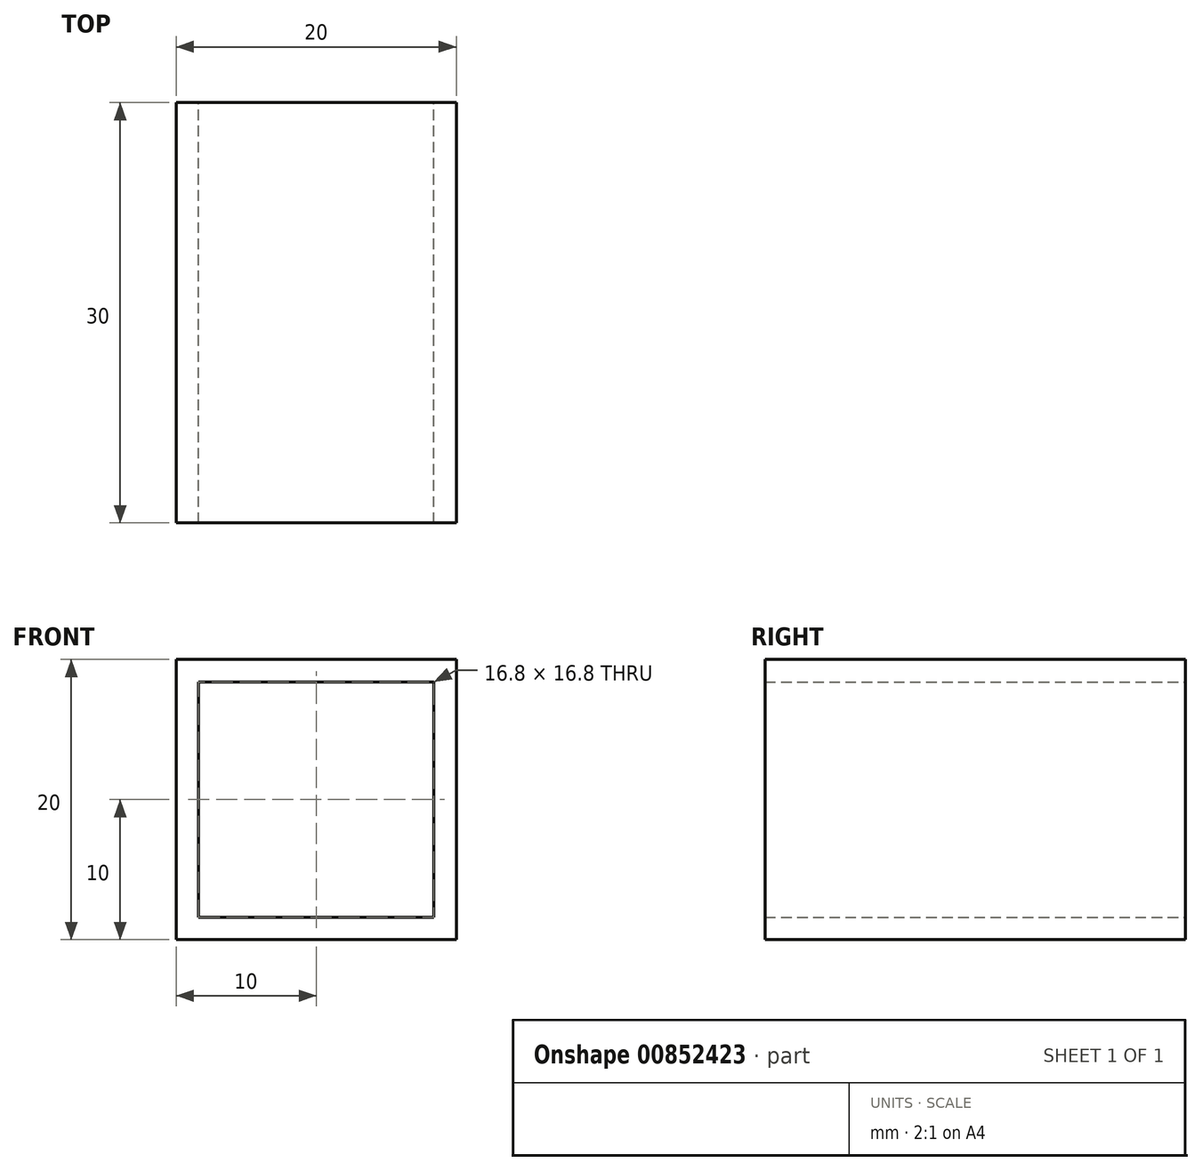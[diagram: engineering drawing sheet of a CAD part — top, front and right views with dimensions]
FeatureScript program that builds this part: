
annotation { "Feature Type Name" : "Feature", "Feature Type Description" : "" }
export const myFeature = defineFeature(function(context is Context, id is Id, definition is map)
    precondition{}
    {
        {
            var Q0;
            Q0=qCreatedBy(makeId("Front.planeOp"),FACE);
            var sketch = newSketch(context, id + "F0", { "sketchPlane" : qUnion([Q0])});
            skLineSegment(sketch, "E0.bottom", {"start": v(10, 10) * mm, "end": v(-10, 10) * mm});
            skLineSegment(sketch, "E0.top", {"start": v(10, -10) * mm, "end": v(-10, -10) * mm});
            skLineSegment(sketch, "E0.left", {"start": v(10, 10) * mm, "end": v(10, -10) * mm});
            skLineSegment(sketch, "E0.right", {"start": v(-10, 10) * mm, "end": v(-10, -10) * mm});
            skPoint(sketch, "E0.middle", {"position": v(0, 0) * mm});
            skLineSegment(sketch, "E1.0", {"start": v(8.4, 8.4) * mm, "end": v(-8.4, 8.4) * mm});
            skLineSegment(sketch, "E1.1", {"start": v(8.4, 8.4) * mm, "end": v(8.4, -8.4) * mm});
            skLineSegment(sketch, "E1.2", {"start": v(8.4, -8.4) * mm, "end": v(-8.4, -8.4) * mm});
            skLineSegment(sketch, "E1.3", {"start": v(-8.4, 8.4) * mm, "end": v(-8.4, -8.4) * mm});
            skSolve(sketch);
        }
        {
            var Q0;
            Q0=makeQuery(id+"F0.imprint","IMPRINT",FACE,{"disambiguationData":[TD([[makeQuery(id+"F0.imprint","IMPRINT",EDGE,{"derivedFrom":sQuery(id+"F0.wireOp",EDGE,"E0.bottom")}),1.0]])]});
            extrude(context, id + "F1", {"entities" : qUnion([Q0]), "depth" : 30 * mm, "offsetDistance" : 25 * mm});
        }
    });
